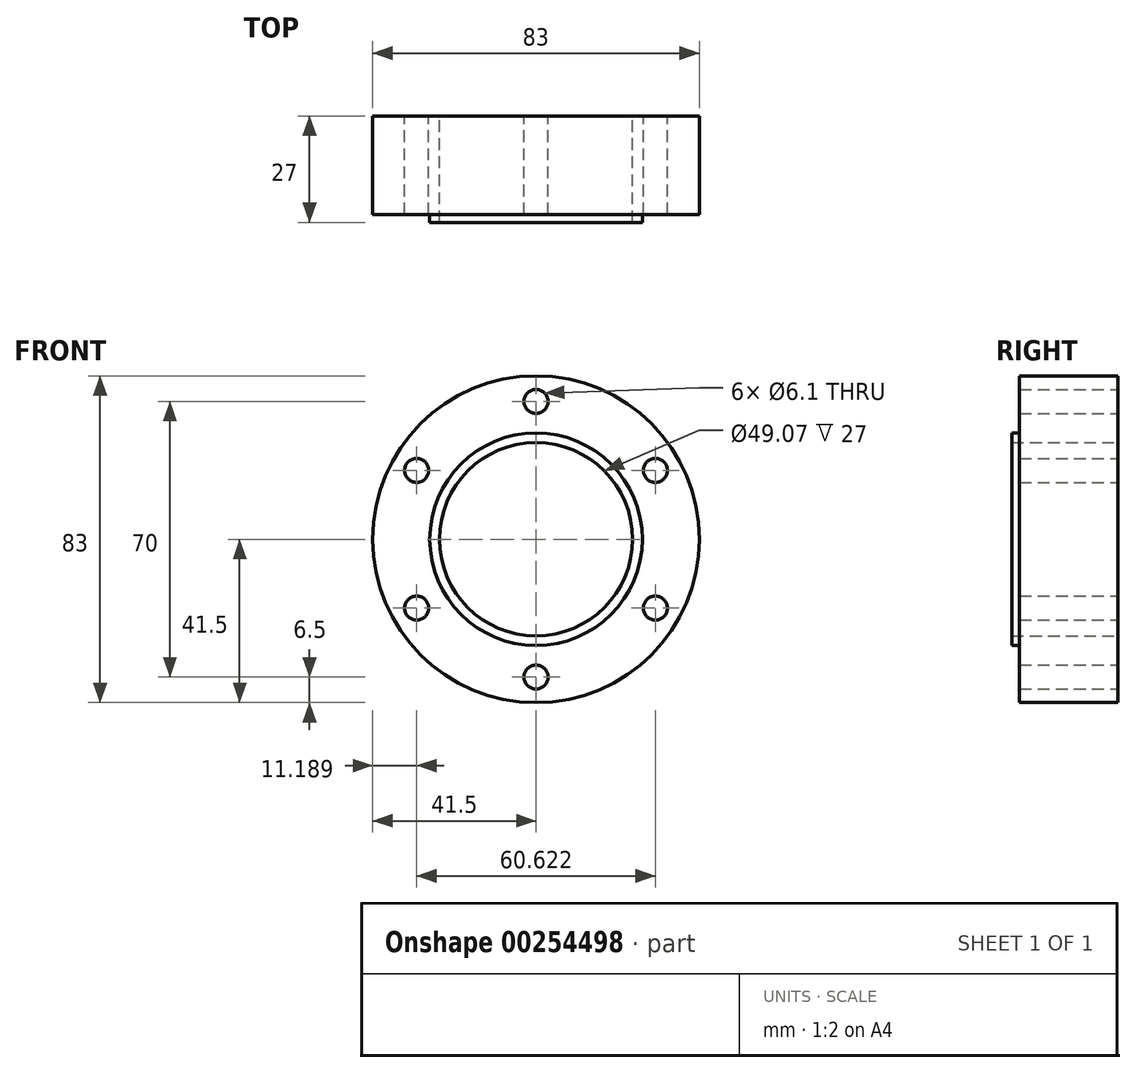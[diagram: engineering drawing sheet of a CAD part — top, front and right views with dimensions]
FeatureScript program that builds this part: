
annotation { "Feature Type Name" : "Feature", "Feature Type Description" : "" }
export const myFeature = defineFeature(function(context is Context, id is Id, definition is map)
    precondition{}
    {
        {
            var Q0;
            Q0=qCreatedBy(makeId("Front.planeOp"),FACE);
            var sketch = newSketch(context, id + "F0", { "sketchPlane" : qUnion([Q0])});
            skCircle(sketch, "E0", {"center": v(0, 0) * mm, "radius": 27 * mm});
            skCircle(sketch, "E1", {"center": v(0, 0) * mm, "radius": 41.5 * mm});
            skCircle(sketch, "E2", {"center": v(0, -35) * mm, "radius": 3.05 * mm});
            skCircle(sketch, "E3", {"center": v(30.31, -17.5) * mm, "radius": 3.05 * mm});
            skCircle(sketch, "E4", {"center": v(30.31, 17.5) * mm, "radius": 3.05 * mm});
            skCircle(sketch, "E5", {"center": v(0, 35) * mm, "radius": 3.05 * mm});
            skCircle(sketch, "E6", {"center": v(-30.31, 17.5) * mm, "radius": 3.05 * mm});
            skCircle(sketch, "E7", {"center": v(-30.31, -17.5) * mm, "radius": 3.05 * mm});
            skLineSegment(sketch, "E8.trimOffspring", {"start": v(32.95, -19.03) * mm, "end": v(33.12, -19.12) * mm});
            skLineSegment(sketch, "E9.trimOffspring", {"start": v(32.95, 19.03) * mm, "end": v(33.01, 19.06) * mm});
            skLineSegment(sketch, "E10", {"start": v(11.51, 39.87) * mm, "end": v(12.48, 43.23) * mm});
            skSolve(sketch);
        }
        {
            var Q0;
            Q0=makeQuery(id+"F0.imprint","IMPRINT",FACE,{"disambiguationData":[TD([[makeQuery(id+"F0.imprint","IMPRINT",EDGE,{"derivedFrom":sQuery(id+"F0.wireOp",EDGE,"E0")}),-1.0]])]});
            extrude(context, id + "F1", {"entities" : qUnion([Q0]), "depth" : 25 * mm});
        }
        {
            var Q0;
            Q0=qCreatedBy(makeId("Front.planeOp"),FACE);
            var sketch = newSketch(context, id + "F2", { "sketchPlane" : qUnion([Q0])});
            skCircle(sketch, "E11", {"center": v(0, 0) * mm, "radius": 27.04 * mm});
            skSolve(sketch);
        }
        {
            var Q0;
            Q0=makeQuery(id+"F0.imprint","IMPRINT",FACE,{"disambiguationData":[TD([[makeQuery(id+"F0.imprint","IMPRINT",EDGE,{"derivedFrom":sQuery(id+"F0.wireOp",EDGE,"E0")}),1.0]])]});
            extrude(context, id + "F3", {"entities" : qUnion([Q0]), "operationType" : NewBodyOperationType.ADD, "depth" : 27 * mm});
        }
        {
            var Q0;
            Q0=qCreatedBy(makeId("Front.planeOp"),FACE);
            var sketch = newSketch(context, id + "F4", { "sketchPlane" : qUnion([Q0])});
            skCircle(sketch, "E12", {"center": v(0, 0) * mm, "radius": 24.54 * mm});
            skSolve(sketch);
        }
        {
            var Q0;
            Q0=makeQuery(id+"F4.imprint","IMPRINT",FACE,{"disambiguationData":[TD([[makeQuery(id+"F4.imprint","IMPRINT",EDGE,{"derivedFrom":sQuery(id+"F4.wireOp",EDGE,"E12")}),1.0]])]});
            extrude(context, id + "F5", {"entities" : qUnion([Q0]), "operationType" : NewBodyOperationType.REMOVE, "depth" : 27 * mm});
        }
    });
